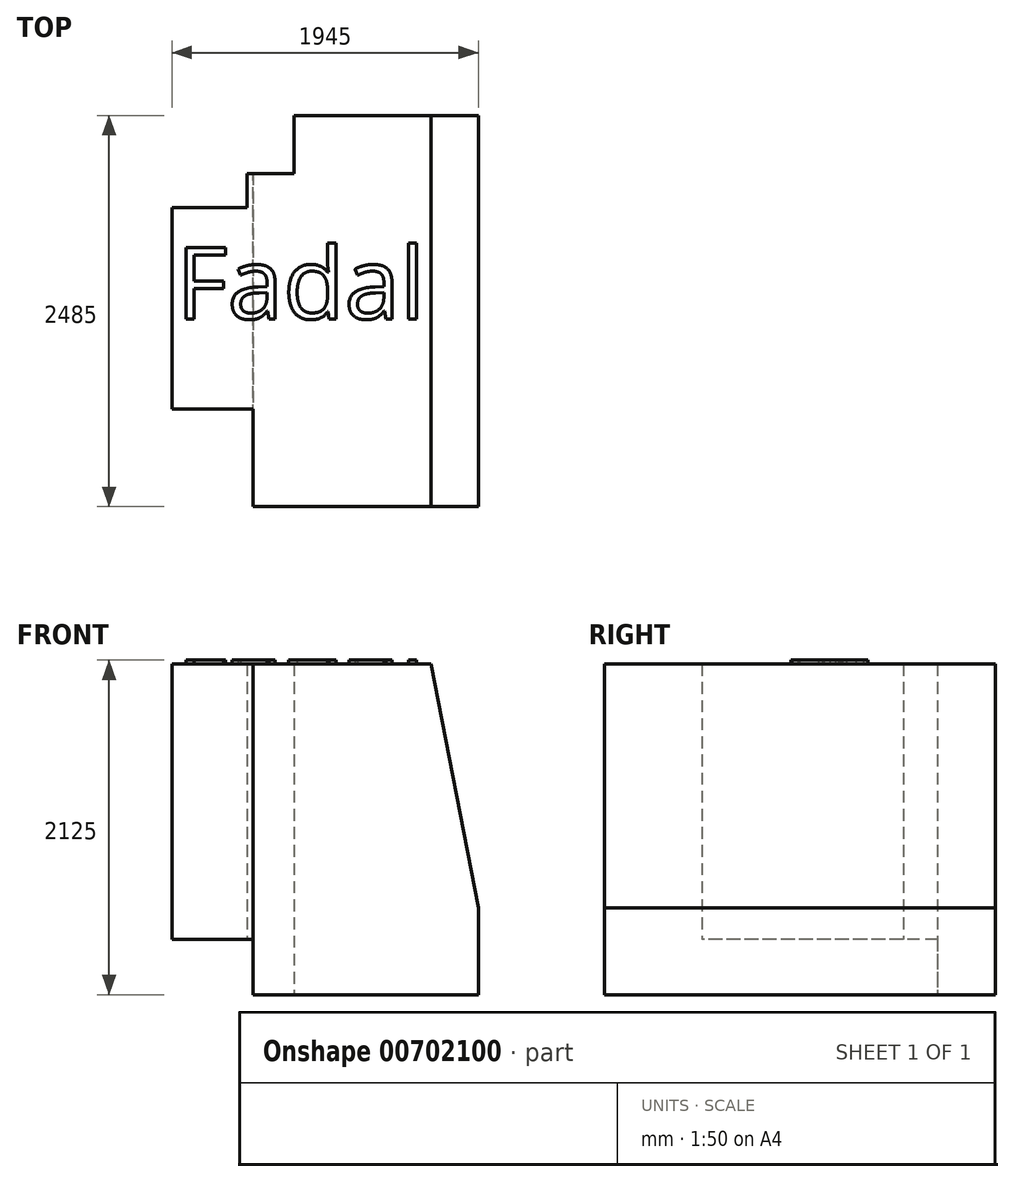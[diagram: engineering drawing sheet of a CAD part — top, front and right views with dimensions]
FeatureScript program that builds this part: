
annotation { "Feature Type Name" : "Feature", "Feature Type Description" : "" }
export const myFeature = defineFeature(function(context is Context, id is Id, definition is map)
    precondition{}
    {
        {
            var Q0;
            Q0=qCreatedBy(makeId("Top.planeOp"),FACE);
            var sketch = newSketch(context, id + "F0", { "sketchPlane" : qUnion([Q0])});
            skLineSegment(sketch, "E0.bottom", {"start": v(0, 0) * mm, "end": v(-1430, 0) * mm});
            skLineSegment(sketch, "E0.top", {"start": v(0, 2485) * mm, "end": v(-1170, 2485) * mm});
            skLineSegment(sketch, "E0.left", {"start": v(0, 0) * mm, "end": v(0, 2485) * mm});
            skLineSegment(sketch, "E0.right", {"start": v(-1430, 0) * mm, "end": v(-1430, 620) * mm});
            skLineSegment(sketch, "E1.bottom", {"start": v(-1470, 1900) * mm, "end": v(-1945, 1900) * mm});
            skLineSegment(sketch, "E1.top", {"start": v(-1430, 620) * mm, "end": v(-1945, 620) * mm});
            skLineSegment(sketch, "E1.right", {"start": v(-1945, 1900) * mm, "end": v(-1945, 620) * mm});
            skLineSegment(sketch, "E2", {"start": v(-1170, 2485) * mm, "end": v(-1170, 2115.72) * mm});
            skLineSegment(sketch, "E3", {"start": v(-1170, 2115.72) * mm, "end": v(-1470, 2115.72) * mm});
            skLineSegment(sketch, "E4", {"start": v(-1470, 1900) * mm, "end": v(-1470, 2115.72) * mm});
            skSolve(sketch);
        }
        {
            var Q0;
            Q0=makeQuery(id+"F0.imprint","IMPRINT",FACE,{"disambiguationData":[TD([[makeQuery(id+"F0.imprint","IMPRINT",EDGE,{"derivedFrom":sQuery(id+"F0.wireOp",EDGE,"E0.bottom")}),-1.0]])]});
            extrude(context, id + "F1", {"entities" : qUnion([Q0]), "depth" : 2100 * mm, "offsetDistance" : 25 * mm});
        }
        {
            var Q0;
            Q0=makeQuery(id+"F1.opExtrude","SWEPT_FACE",FACE,{"disambiguationData":[OSD([sQuery(id+"F0.wireOp",EDGE,"E0.bottom")])]});
            var sketch = newSketch(context, id + "F2", { "sketchPlane" : qUnion([Q0])});
            skLineSegment(sketch, "E5", {"start": v(0, 550) * mm, "end": v(-300, 2100) * mm});
            skLineSegment(sketch, "E6", {"start": v(-300, 2100) * mm, "end": v(0, 2100) * mm});
            skLineSegment(sketch, "E7", {"start": v(0, 2100) * mm, "end": v(0, 550) * mm});
            skSolve(sketch);
        }
        {
            var Q0;
            Q0=makeQuery(id+"F2.imprint","IMPRINT",FACE,{"disambiguationData":[TD([[makeQuery(id+"F2.imprint","IMPRINT",EDGE,{"derivedFrom":sQuery(id+"F2.wireOp",EDGE,"E5")}),-1.0]])]});
            extrude(context, id + "F3", {"entities" : qUnion([Q0]), "operationType" : NewBodyOperationType.REMOVE, "endBound" : BoundingType.THROUGH_ALL, "oppositeDirection" : true, "depth" : 25 * mm, "offsetDistance" : 25 * mm});
        }
        {
            var Q0;
            Q0=makeQuery(id+"F1.opExtrude","SWEPT_FACE",FACE,{"disambiguationData":[OSD([sQuery(id+"F0.wireOp",EDGE,"E1.top")])]});
            var sketch = newSketch(context, id + "F4", { "sketchPlane" : qUnion([Q0])});
            skLineSegment(sketch, "E8.bottom", {"start": v(-1945, 0) * mm, "end": v(-1430, 0) * mm});
            skLineSegment(sketch, "E8.top", {"start": v(-1945, 350) * mm, "end": v(-1430, 350) * mm});
            skLineSegment(sketch, "E8.left", {"start": v(-1945, 0) * mm, "end": v(-1945, 350) * mm});
            skLineSegment(sketch, "E8.right", {"start": v(-1430, 0) * mm, "end": v(-1430, 350) * mm});
            skSolve(sketch);
        }
        {
            var Q0;
            Q0=makeQuery(id+"F4.imprint","IMPRINT",FACE,{"disambiguationData":[TD([[makeQuery(id+"F4.imprint","IMPRINT",EDGE,{"derivedFrom":sQuery(id+"F4.wireOp",EDGE,"E8.bottom")}),-1.0]])]});
            extrude(context, id + "F5", {"entities" : qUnion([Q0]), "operationType" : NewBodyOperationType.REMOVE, "endBound" : BoundingType.THROUGH_ALL, "oppositeDirection" : true, "depth" : 25 * mm, "offsetDistance" : 25 * mm});
        }
        {
            var Q0;
            Q0=makeQuery(id+"F1.opExtrude","CAP_FACE",FACE,{"disambiguationData":[OSD([sQuery(id+"F0.wireOp",EDGE,"E0.bottom"),sQuery(id+"F0.wireOp",EDGE,"E0.top"),sQuery(id+"F0.wireOp",EDGE,"E0.left"),sQuery(id+"F0.wireOp",EDGE,"E0.right"),sQuery(id+"F0.wireOp",EDGE,"E1.bottom"),sQuery(id+"F0.wireOp",EDGE,"E1.top"),sQuery(id+"F0.wireOp",EDGE,"E1.right"),sQuery(id+"F0.wireOp",EDGE,"E2"),sQuery(id+"F0.wireOp",EDGE,"E3"),sQuery(id+"F0.wireOp",EDGE,"E4")])],"isStart":false});
            var sketch = newSketch(context, id + "F6", { "sketchPlane" : qUnion([Q0])});
            skText(sketch, "E9", { "text": "Fadal", "fontName": "OpenSans-Regular.ttf"});
            const initialGuessF6  = {"E9": [-1.92, 1.1929, 1, 0, 0.4571]};
            skSetInitialGuess(sketch, initialGuessF6);
            skSolve(sketch);
        }
        {
            var Q0;
            Q0 = qSketchRegion(id + "F6", true);
            extrude(context, id + "F7", {"entities" : qUnion([Q0]), "operationType" : NewBodyOperationType.ADD, "depth" : 25 * mm, "offsetDistance" : 25 * mm});
        }
    });
